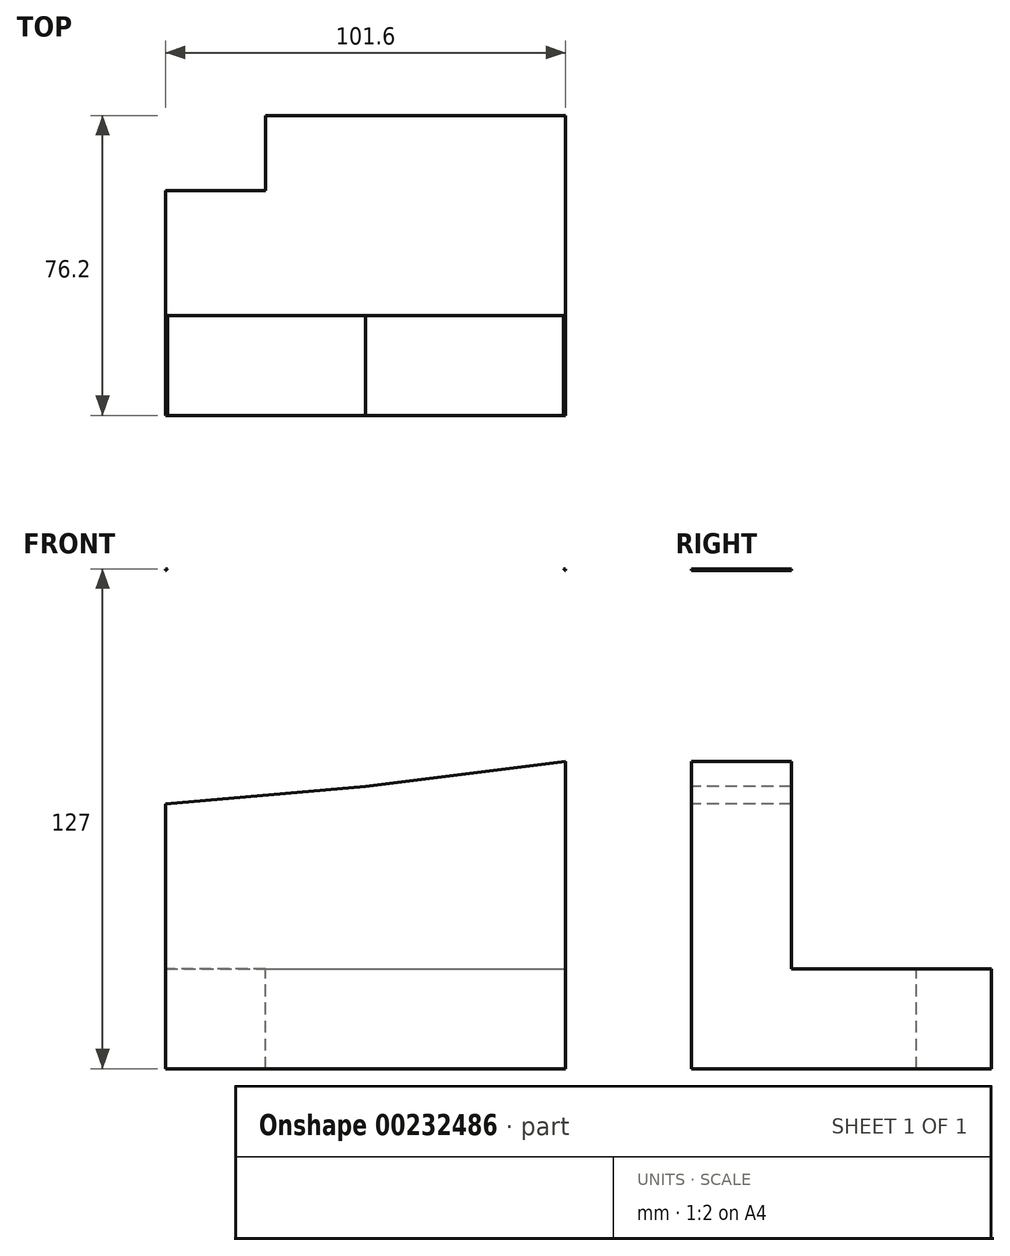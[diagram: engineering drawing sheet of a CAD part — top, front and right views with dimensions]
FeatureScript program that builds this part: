
annotation { "Feature Type Name" : "Feature", "Feature Type Description" : "" }
export const myFeature = defineFeature(function(context is Context, id is Id, definition is map)
    precondition{}
    {
        {
            var Q0;
            Q0=qCreatedBy(makeId("Top.planeOp"),FACE);
            var sketch = newSketch(context, id + "F0", { "sketchPlane" : qUnion([Q0])});
            skLineSegment(sketch, "E0.bottom", {"start": v(-50.8, 0) * mm, "end": v(50.8, 0) * mm});
            skLineSegment(sketch, "E0.top", {"start": v(-50.8, -25.4) * mm, "end": v(50.8, -25.4) * mm});
            skLineSegment(sketch, "E0.left", {"start": v(-50.8, 0) * mm, "end": v(-50.8, -25.4) * mm});
            skLineSegment(sketch, "E0.right", {"start": v(50.8, 0) * mm, "end": v(50.8, -25.4) * mm});
            skSolve(sketch);
        }
        {
            var Q0;
            Q0=makeQuery(id+"F0.imprint","IMPRINT",FACE,{"disambiguationData":[TD([[makeQuery(id+"F0.imprint","IMPRINT",EDGE,{"derivedFrom":sQuery(id+"F0.wireOp",EDGE,"E0.bottom")}),-1.0]])]});
            extrude(context, id + "F1", {"entities" : qUnion([Q0]), "endBound" : BoundingType.SYMMETRIC, "depth" : 127 * mm});
        }
        {
            var Q0;
            Q0=qCreatedBy(makeId("Front.planeOp"),FACE);
            var sketch = newSketch(context, id + "F2", { "sketchPlane" : qUnion([Q0])});
            skLineSegment(sketch, "E1.bottom", {"start": v(-50.8, -63.5) * mm, "end": v(50.8, -63.5) * mm});
            skLineSegment(sketch, "E1.top", {"start": v(-50.8, -38.1) * mm, "end": v(50.8, -38.1) * mm});
            skLineSegment(sketch, "E1.left", {"start": v(-50.8, -63.5) * mm, "end": v(-50.8, -38.1) * mm});
            skLineSegment(sketch, "E1.right", {"start": v(50.8, -63.5) * mm, "end": v(50.8, -38.1) * mm});
            skSolve(sketch);
        }
        {
            var Q0;
            Q0=makeQuery(id+"F2.imprint","IMPRINT",FACE,{"disambiguationData":[TD([[makeQuery(id+"F2.imprint","IMPRINT",EDGE,{"derivedFrom":sQuery(id+"F2.wireOp",EDGE,"E1.bottom")}),1.0]])]});
            extrude(context, id + "F3", {"entities" : qUnion([Q0]), "operationType" : NewBodyOperationType.ADD, "oppositeDirection" : true, "depth" : 50.8 * mm});
        }
        {
            var Q0;
            Q0=qCreatedBy(makeId("Top.planeOp"),FACE);
            var sketch = newSketch(context, id + "F4", { "sketchPlane" : qUnion([Q0])});
            skLineSegment(sketch, "E2.bottom", {"start": v(-50.8, 50.8) * mm, "end": v(-25.4, 50.8) * mm});
            skLineSegment(sketch, "E2.top", {"start": v(-50.8, 31.75) * mm, "end": v(-25.4, 31.75) * mm});
            skLineSegment(sketch, "E2.left", {"start": v(-50.8, 50.8) * mm, "end": v(-50.8, 31.75) * mm});
            skLineSegment(sketch, "E2.right", {"start": v(-25.4, 50.8) * mm, "end": v(-25.4, 31.75) * mm});
            skSolve(sketch);
        }
        {
            var Q0;
            Q0=makeQuery(id+"F4.imprint","IMPRINT",FACE,{"disambiguationData":[TD([[makeQuery(id+"F4.imprint","IMPRINT",EDGE,{"derivedFrom":sQuery(id+"F4.wireOp",EDGE,"E2.bottom")}),-1.0]])]});
            extrude(context, id + "F5", {"entities" : qUnion([Q0]), "operationType" : NewBodyOperationType.REMOVE, "oppositeDirection" : true, "depth" : 127 * mm});
        }
        {
            var Q0;
            Q0=qCreatedBy(makeId("Right.planeOp"),FACE);
            var sketch = newSketch(context, id + "F6", { "sketchPlane" : qUnion([Q0])});
            skLineSegment(sketch, "E3.bottom", {"start": v(0, 8.18) * mm, "end": v(-25.4, 8.18) * mm});
            skLineSegment(sketch, "E3.top", {"start": v(0, 82.94) * mm, "end": v(-25.4, 82.94) * mm});
            skLineSegment(sketch, "E3.left", {"start": v(0, 8.18) * mm, "end": v(0, 82.94) * mm});
            skLineSegment(sketch, "E3.right", {"start": v(-25.4, 8.18) * mm, "end": v(-25.4, 82.94) * mm});
            skSolve(sketch);
        }
        {
            var Q0;
            Q0 = qSketchRegion(id + "F6", true);
            var Q1;
            Q1=sQuery(id+"F6.wireOp",EDGE,"E3.bottom");
            revolve(context, id + "F7", {"operationType" : NewBodyOperationType.REMOVE, "entities" : qUnion([Q0]), "axis" : qUnion([Q1]), "revolveType" : RevolveType.TWO_DIRECTIONS, "oppositeDirection" : true, "angle" : 82.92 * degree, "angleBack" : 265 * degree});
        }
    });
